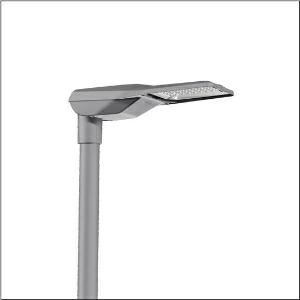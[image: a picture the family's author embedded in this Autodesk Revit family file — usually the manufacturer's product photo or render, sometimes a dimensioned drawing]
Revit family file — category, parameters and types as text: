
# Revit family: streetlight_sl_21_mini___stw1_0a_5xe6e43a08gb_c4a3
name_source: partatom
category: Lighting Fixtures
units: mm (PartAtom-declared; Revit-internal decimal feet)

## family parameters
Cut with Voids When Loaded = No
Host = Face
Light Source = No
Part Type = Normal
Room Calculation Point = No
Round Connector Dimension = Use Diameter
Shared = No

## types (1)
- --- (1 x LED, 6180 lm, 40.4 W, 4000K)
    Apparent Load = 40 VA
    CIE Flux Codes = 38 75 98 100 100
    Color Rendering = 70
    Color Temperature = 4000K
    Default Elevation = 1800 mm
    Description = Streetlight SL 21 mini, mast luminaire, primary light control with lens, of PMMA, primary optical cover: cover, of toughened safety glass, transparent, light distribution: STW1.0a, light emission: direct distribution, primary light characteristic: asymmetric, installation type: post-top, side-entry, LED, 3G 1.5mm², High Power LED, rated luminous flux: 6.180lm, luminous efficacy: 153lm/W, light colour: 740, colour temperature: 4000K, control: overheat protection, constant luminous flux control, time-dependent luminous flux control, flexible luminous flux parameterisation, mains connection: 230..240V, AC, 50/60Hz, connection cable pre-assembled, cable length: 6,5m, wiring characteristics: H07RN-F, start of lifetime: 40W, end of service life: 41W, reduction: 19W, luminaire housing, of diecast aluminium, powder-coated, Siteco® metallic grey (DB 702S), corrosivity category C5 mid according to DIN EN ISO 12944, please order mast flange separately, inclination adjustable: 0°, 5°, 10°, 15°, sealing non-destructively replaceable, multi-level sealing system, length: 628mm, width: 235mm, height: 110mm, mast flange for spigot size: 42mm (side-entry): 5XC10008XM4, 60/48mm (side-entry/post-top): 5XC10108XM2, 76/60mm (side-entry/post-top): 5XC10108XM1, protection rating (complete): IP66, insulation class (complete): insulation class II (safety insulation), certification: CE, ENEC, ENEC+, VDE, impact resistance: IK09, permissible operating ambient temperature for outdoor applications: -40..+50°C, standard-compliant lighting for roads and squares, packaging unit: 1 piece

Light Distribution: STW1.0a
    Height = 110 mm
    Lamp = 1 x LED
    Lamp Light Flux = 6180 lm
    Lamp Power = 40.4 W
    Lamp count = 1
    Length = 625 mm
    Luminous efficacy = 153 lm/W
    Manufacturer = Siteco
    ModVariant = No
    Model = 5XE6E43A08GB
    Number of Poles = 1
    OnlyDefault = Yes
    Power Factor = 1
    Product Name = Streetlight SL 21 mini | STW1.0a
    Product group = mast luminaire | pylon top
    ProductGroupID = 6100
    Protection Class = Protection class II
    Protection Degree = IP 66
    RLX_Detail_Level = 1
    RLX_Emergency_Light_Flux = 0 lm
    RLX_Emergency_Type = 0
    RLX_Emergency_Type_DB = No
    RlxData = <blob elided: 91581 chars, md5=e25eceba>
    Socket = socket
    Standby Power = 0 W
    System Light Flux = 6180 lm
    System Power = 40 W
    Type Comments = factory setting: luminous flux: 100 % | Output Level: 100 % | 812 mA
    Type Image = l_1003519.jpg
    URL = http://relux.com
    VarID = @adj_138873
    Voltage = 0 V
    Weight = 0.00 kg
    Width = 234 mm

## geometry (parser evidence)
native form markers: Blend x4, Sweep x11
no freeform markers — native parametric forms only
